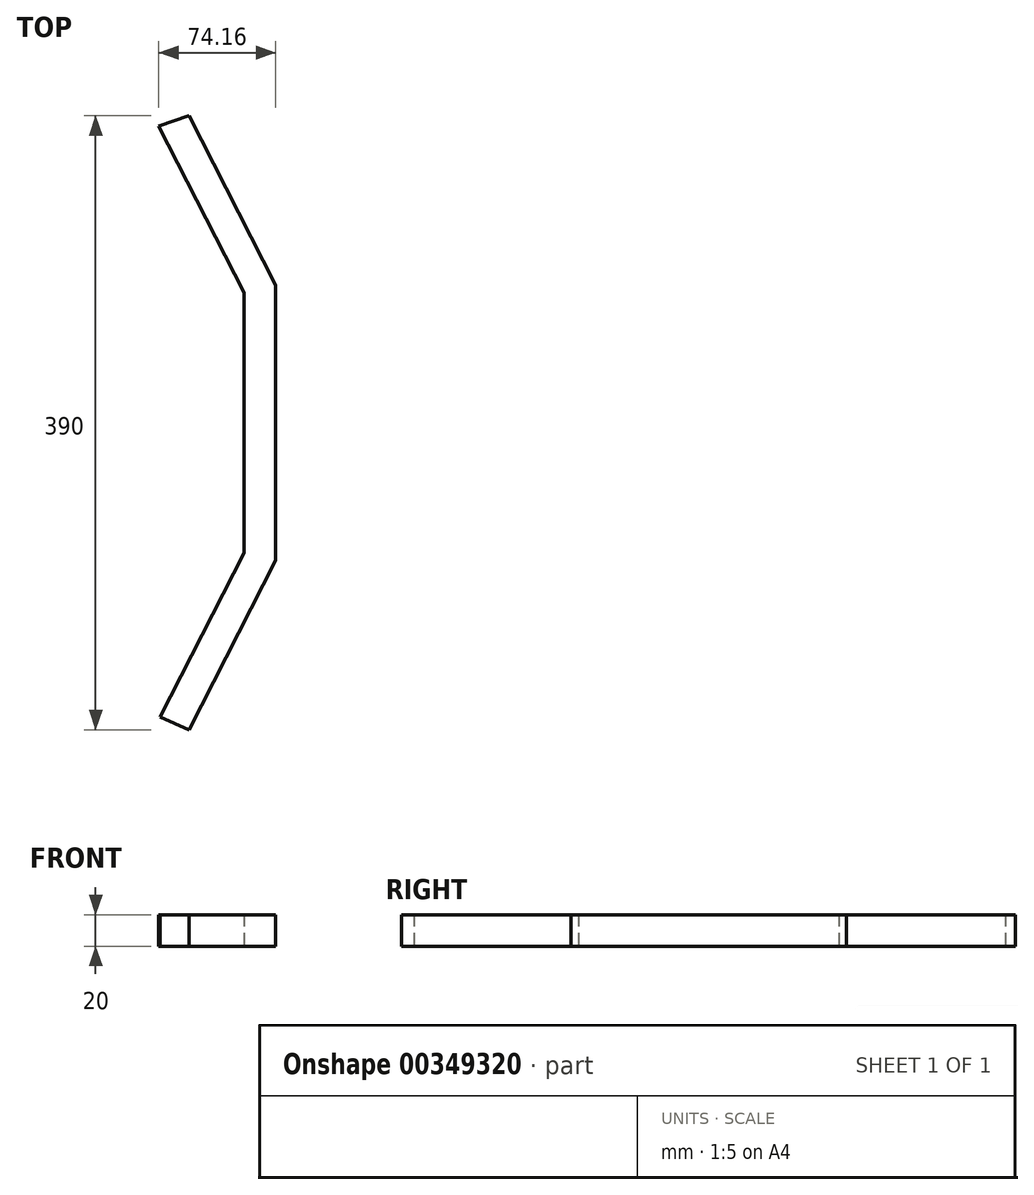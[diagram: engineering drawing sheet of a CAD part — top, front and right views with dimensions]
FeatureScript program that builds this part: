
annotation { "Feature Type Name" : "Feature", "Feature Type Description" : "" }
export const myFeature = defineFeature(function(context is Context, id is Id, definition is map)
    precondition{}
    {
        {
            var Q0;
            Q0=qCreatedBy(makeId("Top.planeOp"),FACE);
            var sketch = newSketch(context, id + "F0", { "sketchPlane" : qUnion([Q0])});
            skLineSegment(sketch, "E0", {"start": v(27.5, 0) * mm, "end": v(27.5, 87.5) * mm});
            skLineSegment(sketch, "E1", {"start": v(27.5, 87.5) * mm, "end": v(-27.5, 195) * mm});
            skLineSegment(sketch, "E2", {"start": v(5.39, 130.72) * mm, "end": v(-12.42, 121.6) * mm});
            skLineSegment(sketch, "E3", {"start": v(27.5, 0) * mm, "end": v(7.5, 0) * mm});
            skLineSegment(sketch, "E4", {"start": v(27.5, 0) * mm, "end": v(27.5, -87.5) * mm});
            skLineSegment(sketch, "E5", {"start": v(-27.5, -195) * mm, "end": v(27.5, -87.5) * mm});
            skLineSegment(sketch, "E6", {"start": v(7.5, 0) * mm, "end": v(7.5, 236.53) * mm});
            skLineSegment(sketch, "E7", {"start": v(7.5, 0) * mm, "end": v(7.5, -90.56) * mm});
            skLineSegment(sketch, "E8", {"start": v(0, -141.25) * mm, "end": v(-17.8, -132.14) * mm});
            skLineSegment(sketch, "E9", {"start": v(-17.8, -132.14) * mm, "end": v(-45.88, -187.02) * mm});
            skLineSegment(sketch, "E10", {"start": v(-17.8, -132.14) * mm, "end": v(22.86, -52.67) * mm});
            skLineSegment(sketch, "E11", {"start": v(-45.88, -187.02) * mm, "end": v(-27.5, -195) * mm});
            skLineSegment(sketch, "E12", {"start": v(-12.42, 121.6) * mm, "end": v(7.5, 82.68) * mm});
            skLineSegment(sketch, "E13", {"start": v(-12.42, 121.6) * mm, "end": v(-46.66, 188.53) * mm});
            skLineSegment(sketch, "E14", {"start": v(-46.66, 188.53) * mm, "end": v(-27.5, 195) * mm});
            skSolve(sketch);
        }
        {
            var Q0;
            {var subQ2=sQuery(id+"F0.wireOp",EDGE,"E2");Q0=makeQuery(id+"F0.imprint","IMPRINT",FACE,{"disambiguationData":[TD([[makeQuery(id+"F0.imprint","IMPRINT",EDGE,{"derivedFrom":subQ2}),-1.0]])]});}
            var Q1;
            {var subQ0=sQuery(id+"F0.wireOp",EDGE,"E2");Q1=makeQuery(id+"F0.imprint","IMPRINT",FACE,{"disambiguationData":[TD([[makeQuery(id+"F0.imprint","IMPRINT",EDGE,{"derivedFrom":subQ0}),1.0]])]});}
            var Q2;
            {var subQ4=sQuery(id+"F0.wireOp",EDGE,"E0");Q2=makeQuery(id+"F0.imprint","IMPRINT",FACE,{"disambiguationData":[TD([[makeQuery(id+"F0.imprint","IMPRINT",EDGE,{"derivedFrom":subQ4}),1.0]])]});}
            var Q3;
            {var subQ4=sQuery(id+"F0.wireOp",EDGE,"E3");Q3=makeQuery(id+"F0.imprint","IMPRINT",FACE,{"disambiguationData":[TD([[makeQuery(id+"F0.imprint","IMPRINT",EDGE,{"derivedFrom":subQ4}),1.0]])]});}
            var Q4;
            {var subQ2=sQuery(id+"F0.wireOp",EDGE,"E8");Q4=makeQuery(id+"F0.imprint","IMPRINT",FACE,{"disambiguationData":[TD([[makeQuery(id+"F0.imprint","IMPRINT",EDGE,{"derivedFrom":subQ2}),1.0]])]});}
            extrude(context, id + "F1", {"entities" : qUnion([Q0, Q1, Q2, Q3, Q4]), "endBound" : BoundingType.SYMMETRIC, "depth" : 20 * mm});
        }
    });
